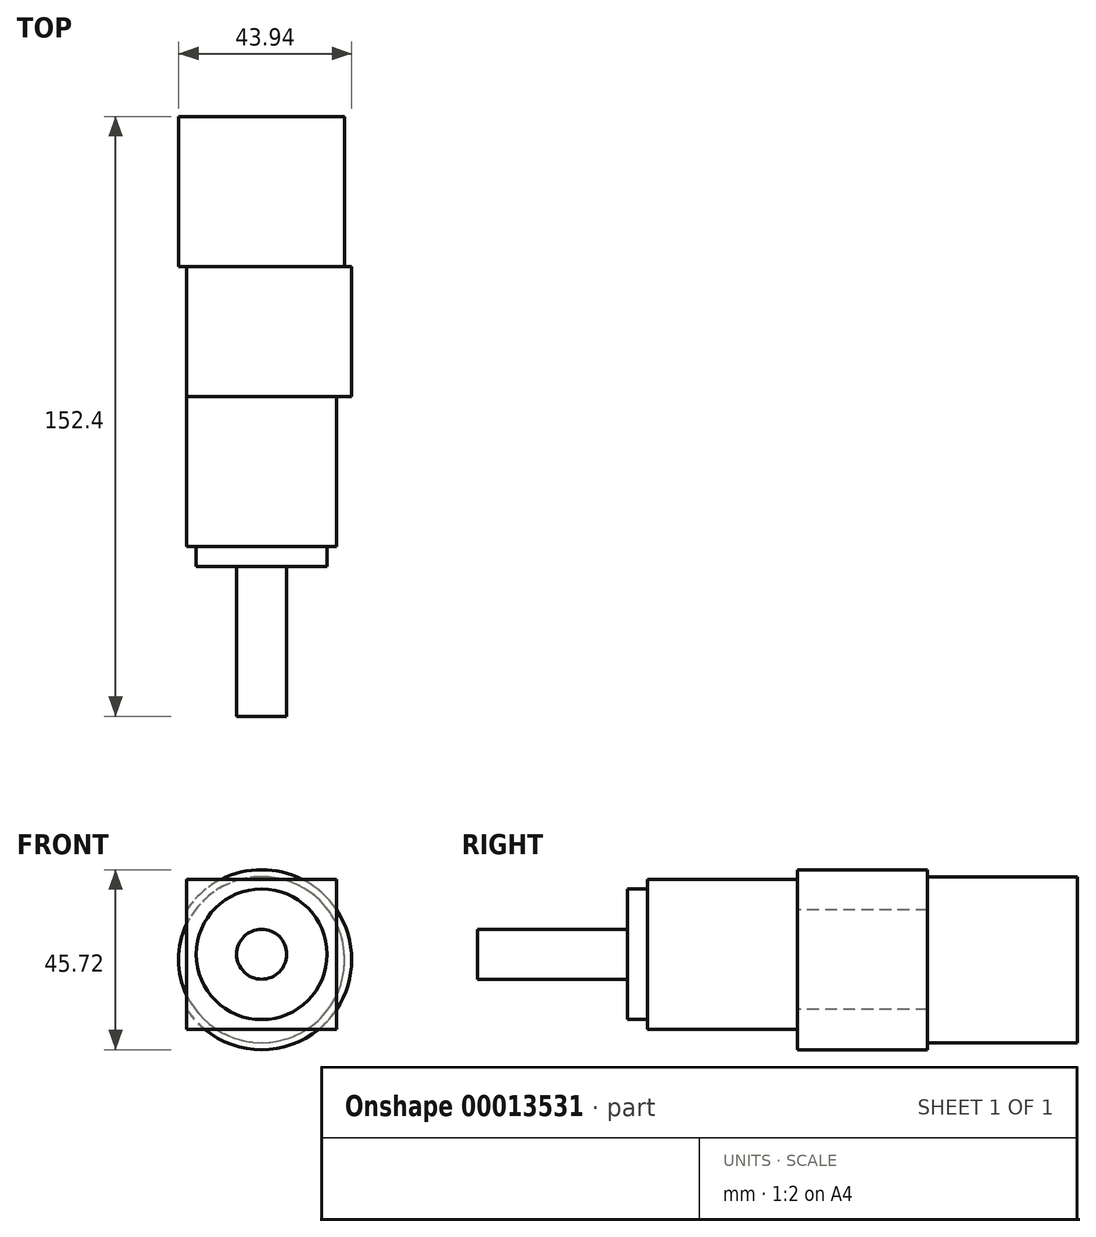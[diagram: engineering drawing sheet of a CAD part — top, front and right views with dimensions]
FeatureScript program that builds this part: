
annotation { "Feature Type Name" : "Feature", "Feature Type Description" : "" }
export const myFeature = defineFeature(function(context is Context, id is Id, definition is map)
    precondition{}
    {
        {
            var Q0;
            Q0=qCreatedBy(makeId("Front.planeOp"),FACE);
            var sketch = newSketch(context, id + "F0", { "sketchPlane" : qUnion([Q0])});
            skLineSegment(sketch, "E0.bottom", {"start": v(0, 0) * mm, "end": v(38.1, 0) * mm});
            skLineSegment(sketch, "E0.top", {"start": v(0, 38.1) * mm, "end": v(38.1, 38.1) * mm});
            skLineSegment(sketch, "E0.left", {"start": v(0, 0) * mm, "end": v(0, 38.1) * mm});
            skLineSegment(sketch, "E0.right", {"start": v(38.1, 0) * mm, "end": v(38.1, 38.1) * mm});
            skSolve(sketch);
        }
        {
            var Q0;
            Q0=makeQuery(id+"F0.imprint","IMPRINT",FACE,{"disambiguationData":[TD([[makeQuery(id+"F0.imprint","IMPRINT",EDGE,{"derivedFrom":sQuery(id+"F0.wireOp",EDGE,"E0.bottom")}),1.0]])]});
            extrude(context, id + "F1", {"entities" : qUnion([Q0]), "depth" : 38.1 * mm});
        }
        {
            var Q0;
            Q0=makeQuery(id+"F1.opExtrude","CAP_FACE",FACE,{"disambiguationData":[OSD([sQuery(id+"F0.wireOp",EDGE,"E0.bottom"),sQuery(id+"F0.wireOp",EDGE,"E0.top"),sQuery(id+"F0.wireOp",EDGE,"E0.left"),sQuery(id+"F0.wireOp",EDGE,"E0.right")])],"isStart":false});
            var sketch = newSketch(context, id + "F2", { "sketchPlane" : qUnion([Q0])});
            skCircle(sketch, "E1", {"center": v(19.05, 19.05) * mm, "radius": 16.6 * mm});
            skSolve(sketch);
        }
        {
            var Q0;
            Q0=makeQuery(id+"F2.imprint","IMPRINT",FACE,{"disambiguationData":[TD([[makeQuery(id+"F2.imprint","IMPRINT",EDGE,{"derivedFrom":sQuery(id+"F2.wireOp",EDGE,"E1")}),1.0]])]});
            extrude(context, id + "F3", {"entities" : qUnion([Q0]), "operationType" : NewBodyOperationType.ADD, "depth" : 5.08 * mm});
        }
        {
            var Q0;
            Q0=makeQuery(id+"F3.opExtrude","CAP_FACE",FACE,{"disambiguationData":[OSD([sQuery(id+"F2.wireOp",EDGE,"E1")])],"isStart":false});
            var sketch = newSketch(context, id + "F4", { "sketchPlane" : qUnion([Q0])});
            skCircle(sketch, "E2", {"center": v(19.05, 19.05) * mm, "radius": 6.35 * mm});
            skSolve(sketch);
        }
        {
            var Q0;
            Q0=makeQuery(id+"F4.imprint","IMPRINT",FACE,{"disambiguationData":[TD([[makeQuery(id+"F4.imprint","IMPRINT",EDGE,{"derivedFrom":sQuery(id+"F4.wireOp",EDGE,"E2")}),1.0]])]});
            extrude(context, id + "F5", {"entities" : qUnion([Q0]), "operationType" : NewBodyOperationType.ADD, "depth" : 38.1 * mm});
        }
        {
            var Q0;
            Q0=makeQuery(id+"F1.opExtrude","CAP_FACE",FACE,{"disambiguationData":[OSD([sQuery(id+"F0.wireOp",EDGE,"E0.bottom"),sQuery(id+"F0.wireOp",EDGE,"E0.top"),sQuery(id+"F0.wireOp",EDGE,"E0.left"),sQuery(id+"F0.wireOp",EDGE,"E0.right")])],"isStart":true});
            var sketch = newSketch(context, id + "F6", { "sketchPlane" : qUnion([Q0])});
            skCircle(sketch, "E3", {"center": v(-19.05, 17.66) * mm, "radius": 22.86 * mm});
            skSolve(sketch);
        }
        {
            var Q0;
            {var subQ0=makeQuery(id+"F1.opExtrude","CAP_EDGE",EDGE,{"disambiguationData":[OSD([sQuery(id+"F0.wireOp",EDGE,"E0.top")])],"isStart":true});var subQ1=sQuery(id+"F6.wireOp",EDGE,"E3");var subQ3=makeQuery(id+"F6.imprint","INTERSECT",VERTEX,{"disambiguationData":[OD(0.0)],"derivedFrom":[subQ0,subQ1]});Q0=makeQuery(id+"F6.imprint","IMPRINT",FACE,{"disambiguationData":[TD([[makeQuery(id+"F6.imprint","IMPRINT",EDGE,{"disambiguationData":[TD([[subQ3,-1.0]])],"derivedFrom":subQ1}),1.0]])]});}
            var Q1;
            {var subQ0=makeQuery(id+"F1.opExtrude","CAP_EDGE",EDGE,{"disambiguationData":[OSD([sQuery(id+"F0.wireOp",EDGE,"E0.right")])],"isStart":true});var subQ1=sQuery(id+"F6.wireOp",EDGE,"E3");var subQ3=makeQuery(id+"F6.imprint","INTERSECT",VERTEX,{"disambiguationData":[OD(0.0)],"derivedFrom":[subQ0,subQ1]});Q1=makeQuery(id+"F6.imprint","IMPRINT",FACE,{"disambiguationData":[TD([[makeQuery(id+"F6.imprint","IMPRINT",EDGE,{"disambiguationData":[TD([[subQ3,-1.0]])],"derivedFrom":subQ1}),1.0]])]});}
            var Q2;
            {var subQ0=makeQuery(id+"F1.opExtrude","CAP_EDGE",EDGE,{"disambiguationData":[OSD([sQuery(id+"F0.wireOp",EDGE,"E0.bottom")])],"isStart":true});var subQ1=sQuery(id+"F6.wireOp",EDGE,"E3");var subQ3=makeQuery(id+"F6.imprint","INTERSECT",VERTEX,{"disambiguationData":[OD(0.0)],"derivedFrom":[subQ0,subQ1]});Q2=makeQuery(id+"F6.imprint","IMPRINT",FACE,{"disambiguationData":[TD([[makeQuery(id+"F6.imprint","IMPRINT",EDGE,{"disambiguationData":[TD([[subQ3,-1.0]])],"derivedFrom":subQ1}),1.0]])]});}
            var Q3;
            {var subQ0=makeQuery(id+"F1.opExtrude","CAP_EDGE",EDGE,{"disambiguationData":[OSD([sQuery(id+"F0.wireOp",EDGE,"E0.left")])],"isStart":true});var subQ1=sQuery(id+"F6.wireOp",EDGE,"E3");var subQ3=makeQuery(id+"F6.imprint","INTERSECT",VERTEX,{"disambiguationData":[OD(0.0)],"derivedFrom":[subQ0,subQ1]});Q3=makeQuery(id+"F6.imprint","IMPRINT",FACE,{"disambiguationData":[TD([[makeQuery(id+"F6.imprint","IMPRINT",EDGE,{"disambiguationData":[TD([[subQ3,1.0]])],"derivedFrom":subQ1}),1.0]])]});}
            var Q4;
            {var subQ1=sQuery(id+"F6.wireOp",EDGE,"E3");var subQ4=makeQuery(id+"F1.opExtrude","CAP_EDGE",EDGE,{"disambiguationData":[OSD([sQuery(id+"F0.wireOp",EDGE,"E0.top")])],"isStart":true});var subQ6=makeQuery(id+"F6.imprint","INTERSECT",VERTEX,{"disambiguationData":[OD(0.0)],"derivedFrom":[subQ4,subQ1]});Q4=makeQuery(id+"F6.imprint","IMPRINT",FACE,{"disambiguationData":[TD([[makeQuery(id+"F6.imprint","IMPRINT",EDGE,{"disambiguationData":[TD([[subQ6,1.0]])],"derivedFrom":subQ1}),1.0]])]});}
            extrude(context, id + "F7", {"entities" : qUnion([Q0, Q1, Q2, Q3, Q4]), "operationType" : NewBodyOperationType.ADD, "depth" : 33.02 * mm});
        }
        {
            var Q0;
            Q0=makeQuery(id+"F7.opExtrude","CAP_FACE",FACE,{"disambiguationData":[OSD([sQuery(id+"F6.wireOp",EDGE,"E3")])],"isStart":false});
            var sketch = newSketch(context, id + "F8", { "sketchPlane" : qUnion([Q0])});
            skCircle(sketch, "E4", {"center": v(-19.05, 17.66) * mm, "radius": 21.08 * mm});
            skSolve(sketch);
        }
        {
            var Q0;
            Q0=makeQuery(id+"F8.imprint","IMPRINT",FACE,{"disambiguationData":[TD([[makeQuery(id+"F8.imprint","IMPRINT",EDGE,{"derivedFrom":sQuery(id+"F8.wireOp",EDGE,"E4")}),1.0]])]});
            extrude(context, id + "F9", {"entities" : qUnion([Q0]), "depth" : 38.1 * mm});
        }
    });
